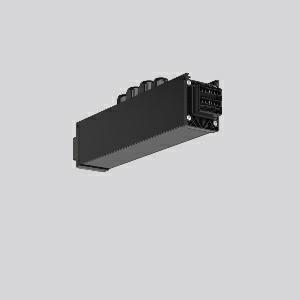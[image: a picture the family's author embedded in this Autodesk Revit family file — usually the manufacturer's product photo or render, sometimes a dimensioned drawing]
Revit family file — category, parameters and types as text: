
# Revit family: linedo_mitteleinspeisung_14pol_s_s_982698_003_2_e364
name_source: partatom
category: Lighting Fixtures
units: mm (PartAtom-declared; Revit-internal decimal feet)

## family parameters
Cut with Voids When Loaded = No
Host = Face
Light Source = No
Part Type = Normal
Room Calculation Point = No
Round Connector Dimension = Use Diameter
Shared = No

## types (1)
- LINEDO_Mitteleinspeisung_14pol_S_S
    Apparent Load = 0 VA
    Default Elevation = 1800 mm
    Description = Series: LINEDO
Middle power feed, 14-pole, connection plug / plug. Housing: extruded aluminium profile, powder-coated. Cover made of plastic, surface like housing. LINEDO plug system, plastic, black. 4 cable glands (2 x M20 and 2 x M25). Cable glands on top. Easy connection for rigid or flexible wires.
Colour: black
Length: 349 mm
Width: 58 mm
Height: 76 mm
Weight: 850 g
    Height = 76 mm
    Lamp = 0 x
    Length = 349 mm
    Luminous efficacy = 0 lm/W
    Manufacturer = RZB
    ModVariant = No
    Model = 982698.003.2
    Mounting Place = Ceiling
    Mounting Type = Pendant, Surface mounted
    Number of Poles = 1
    OnlyDefault = Yes
    Power Factor = 1
    Product Name = LINEDO_Mitteleinspeisung_14pol_S_S
    Product group = Surface mounted continuous line luminaire system
    ProductGroupID = 310
    Protection Class = Protection class I
    Protection Degree = IP 54
    RLX_Detail_Level = 1
    RLX_Emergency_Light_Flux = 0 lm
    RLX_Emergency_Type = 0
    RLX_Emergency_Type_DB = No
    RlxData = <blob elided: 23437 chars, md5=5ddf5859>
    Standby Power = 0 W
    System Light Flux = 0 lm
    System Power = 0 W
    Type Comments = Product without accessories
    Type Image = 982698.003.2.jpg
    URL = http://relux.com
    VarID = ---
    Voltage = 0 V
    Weight = 0.00 kg
    Width = 58 mm

## geometry (parser evidence)
native form markers: Blend x4, Sweep x12
no freeform markers — native parametric forms only
